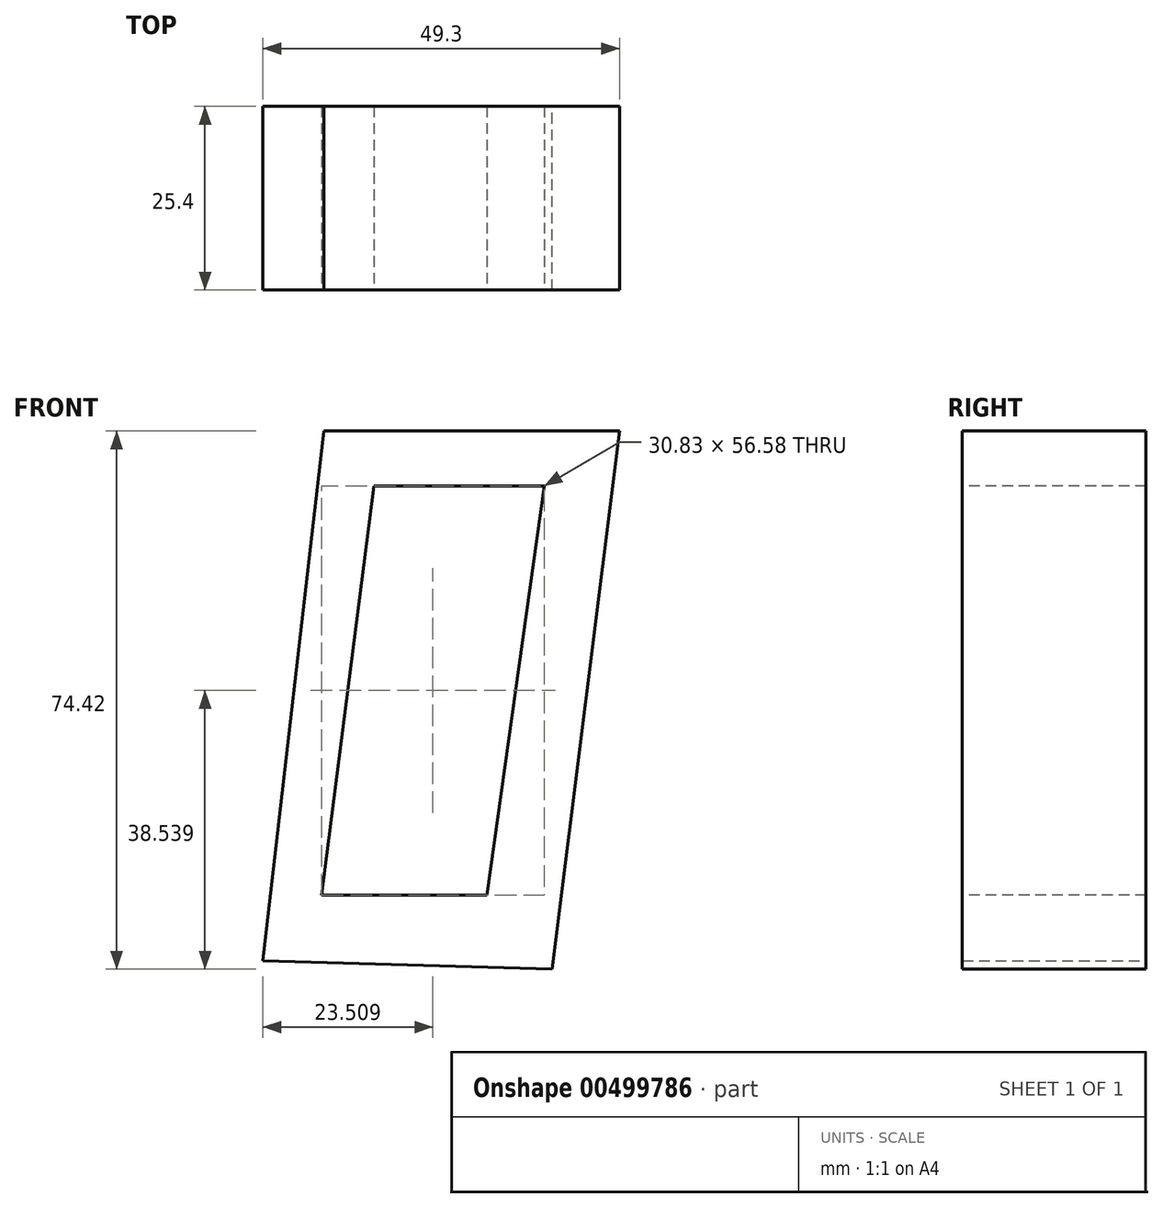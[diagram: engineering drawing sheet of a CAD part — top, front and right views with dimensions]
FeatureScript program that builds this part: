
annotation { "Feature Type Name" : "Feature", "Feature Type Description" : "" }
export const myFeature = defineFeature(function(context is Context, id is Id, definition is map)
    precondition{}
    {
        {
            var Q0;
            Q0=qCreatedBy(makeId("Front.planeOp"),FACE);
            var sketch = newSketch(context, id + "F0", { "sketchPlane" : qUnion([Q0])});
            skLineSegment(sketch, "E0", {"start": v(-18.41, 74.42) * mm, "end": v(22.46, 74.42) * mm});
            skLineSegment(sketch, "E1", {"start": v(-26.84, 1.16) * mm, "end": v(-18.41, 74.42) * mm});
            skLineSegment(sketch, "E2", {"start": v(13.17, 0) * mm, "end": v(22.46, 74.42) * mm});
            skLineSegment(sketch, "E3", {"start": v(-26.84, 1.16) * mm, "end": v(13.17, 0) * mm});
            skSolve(sketch);
        }
        {
            var Q0;
            Q0=makeQuery(id+"F0.imprint","IMPRINT",FACE,{"disambiguationData":[TD([[makeQuery(id+"F0.imprint","IMPRINT",EDGE,{"derivedFrom":sQuery(id+"F0.wireOp",EDGE,"E0")}),-1.0]])]});
            extrude(context, id + "F1", {"entities" : qUnion([Q0]), "depth" : 76.2 * mm});
        }
        {
            var Q0;
            Q0=qCreatedBy(makeId("Front.planeOp"),FACE);
            var sketch = newSketch(context, id + "F2", { "sketchPlane" : qUnion([Q0])});
            skLineSegment(sketch, "E4", {"start": v(-11.5, 66.83) * mm, "end": v(-18.74, 10.25) * mm});
            skLineSegment(sketch, "E5", {"start": v(-18.74, 10.25) * mm, "end": v(4.1, 10.25) * mm});
            skLineSegment(sketch, "E6", {"start": v(4.1, 10.25) * mm, "end": v(12.08, 66.83) * mm});
            skLineSegment(sketch, "E7", {"start": v(12.08, 66.83) * mm, "end": v(-11.5, 66.83) * mm});
            skSolve(sketch);
        }
        {
            var Q0;
            Q0 = qSketchRegion(id + "F2", true);
            var Q1;
            Q1=makeQuery(id+"F1.opExtrude","CAP_FACE",FACE,{"disambiguationData":[OSD([sQuery(id+"F0.wireOp",EDGE,"E0"),sQuery(id+"F0.wireOp",EDGE,"E1"),sQuery(id+"F0.wireOp",EDGE,"E2"),sQuery(id+"F0.wireOp",EDGE,"E3")])],"isStart":false});
            extrude(context, id + "F3", {"entities" : qUnion([Q0, Q1]), "operationType" : NewBodyOperationType.REMOVE, "oppositeDirection" : true, "depth" : 25.4 * mm});
        }
        {
            var Q0;
            Q0 = qSketchRegion(id + "F2", true);
            var Q1;
            Q1=makeQuery(id+"F3.boolean.opBoolean","COPY",FACE,{"derivedFrom":makeQuery(id+"F3.opExtrude","CAP_FACE",FACE,{"disambiguationData":[OSD([sQuery(id+"F0.wireOp",EDGE,"E0"),sQuery(id+"F0.wireOp",EDGE,"E1"),sQuery(id+"F0.wireOp",EDGE,"E2"),sQuery(id+"F0.wireOp",EDGE,"E3")])],"isStart":false})});
            extrude(context, id + "F4", {"entities" : qUnion([Q0, Q1]), "operationType" : NewBodyOperationType.REMOVE, "oppositeDirection" : true, "depth" : 25.4 * mm});
        }
        {
            var Q0;
            Q0 = qSketchRegion(id + "F2", true);
            extrude(context, id + "F5", {"entities" : qUnion([Q0]), "operationType" : NewBodyOperationType.REMOVE, "endBound" : BoundingType.SYMMETRIC, "oppositeDirection" : true, "depth" : 76.2 * mm});
        }
        {
            var Q0;
            Q0=makeQuery(id+"F2.imprint","IMPRINT",FACE,{"disambiguationData":[TD([[makeQuery(id+"F2.imprint","IMPRINT",EDGE,{"derivedFrom":sQuery(id+"F2.wireOp",EDGE,"E4")}),1.0]])]});
            extrude(context, id + "F6", {"entities" : qUnion([Q0]), "operationType" : NewBodyOperationType.ADD, "endBound" : BoundingType.SYMMETRIC, "depth" : 76.2 * mm});
        }
        {
            var Q0;
            Q0=makeQuery(id+"F6.opExtrude","CAP_FACE",FACE,{"disambiguationData":[OSD([sQuery(id+"F2.wireOp",EDGE,"E4"),sQuery(id+"F2.wireOp",EDGE,"E5"),sQuery(id+"F2.wireOp",EDGE,"E6"),sQuery(id+"F2.wireOp",EDGE,"E7")])],"isStart":false});
            extrude(context, id + "F7", {"entities" : qUnion([Q0]), "operationType" : NewBodyOperationType.REMOVE, "endBound" : BoundingType.SYMMETRIC, "oppositeDirection" : true, "depth" : 76.2 * mm});
        }
        {
            var Q0;
            Q0=makeQuery(id+"F6.opExtrude","CAP_FACE",FACE,{"disambiguationData":[OSD([sQuery(id+"F2.wireOp",EDGE,"E4"),sQuery(id+"F2.wireOp",EDGE,"E5"),sQuery(id+"F2.wireOp",EDGE,"E6"),sQuery(id+"F2.wireOp",EDGE,"E7")])],"isStart":true});
            extrude(context, id + "F8", {"entities" : qUnion([Q0]), "operationType" : NewBodyOperationType.REMOVE, "endBound" : BoundingType.SYMMETRIC, "oppositeDirection" : true, "depth" : 76.2 * mm});
        }
        {
            var Q0;
            Q0=makeQuery(id+"F2.imprint","IMPRINT",FACE,{"disambiguationData":[TD([[makeQuery(id+"F2.imprint","IMPRINT",EDGE,{"derivedFrom":sQuery(id+"F2.wireOp",EDGE,"E4")}),1.0]])]});
            extrude(context, id + "F9", {"entities" : qUnion([Q0]), "operationType" : NewBodyOperationType.REMOVE, "endBound" : BoundingType.SYMMETRIC, "oppositeDirection" : true, "depth" : 76.2 * mm});
        }
    });
